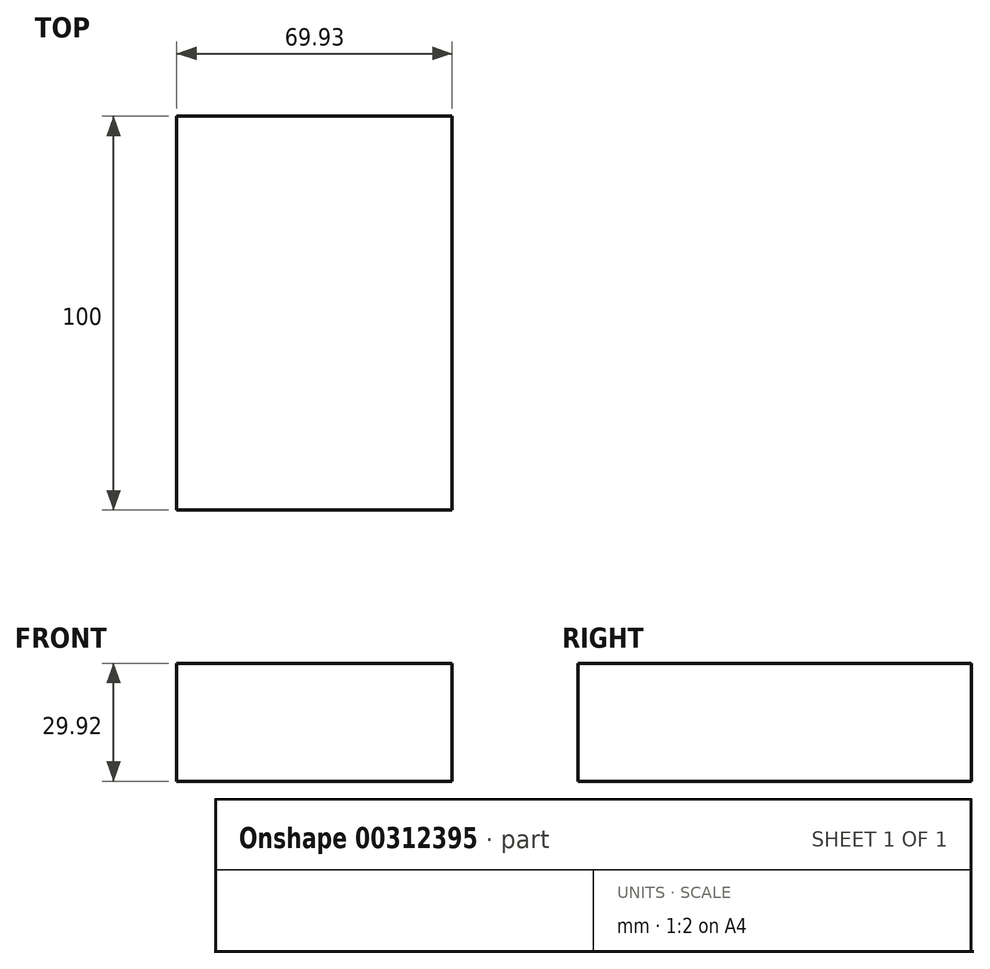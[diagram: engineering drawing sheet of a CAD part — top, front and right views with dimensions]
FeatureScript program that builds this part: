
annotation { "Feature Type Name" : "Feature", "Feature Type Description" : "" }
export const myFeature = defineFeature(function(context is Context, id is Id, definition is map)
    precondition{}
    {
        {
            var Q0;
            Q0=qCreatedBy(makeId("Front.planeOp"),FACE);
            var sketch = newSketch(context, id + "F0", { "sketchPlane" : qUnion([Q0])});
            skLineSegment(sketch, "E0", {"start": v(-56.56, 45.55) * mm, "end": v(13.37, 45.55) * mm});
            skLineSegment(sketch, "E1", {"start": v(13.37, 45.55) * mm, "end": v(13.37, 15.63) * mm});
            skLineSegment(sketch, "E2", {"start": v(13.37, 15.63) * mm, "end": v(-56.56, 15.63) * mm});
            skLineSegment(sketch, "E3", {"start": v(-56.56, 15.63) * mm, "end": v(-56.56, 45.55) * mm});
            skSolve(sketch);
        }
        {
            var Q0;
            Q0=makeQuery(id+"F0.imprint","IMPRINT",FACE,{"disambiguationData":[TD([[makeQuery(id+"F0.imprint","IMPRINT",EDGE,{"derivedFrom":sQuery(id+"F0.wireOp",EDGE,"E0")}),-1.0]])]});
            extrude(context, id + "F1", {"entities" : qUnion([Q0]), "depth" : 100 * mm});
        }
    });
